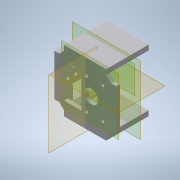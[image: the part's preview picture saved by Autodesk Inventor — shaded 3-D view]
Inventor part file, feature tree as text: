
AUTODESK INVENTOR PART (.ipt)
format: ipt  version: 2022 (Build 260153000, 153)  size: 446,976 bytes
history: native  units: mm
features: other x11, reference x11, sketch x10, plane x9, extrude x9, projected_geometry x4, hole x2, chamfer x1, pattern_linear x1
ambient origin geometry x8: Origin, YZ Plane, XZ Plane, XY Plane, X Axis, Y Axis, Z Axis, Center Point
bodies: Solid1 (feature_tree)
feature tree (58):
  plane  "Work Plane1"
  extrude  "Extrusion1"  Depth=3.0mm
  chamfer  "Chamfer1"  Distance=3.0mm
  sketch  "Sketch2"  dims[d10=3.9mm d11=2.0mm d12=45.0deg d14=31.5mm d15=0.0mm]
  plane  "Work Plane2"
  extrude  "Extrusion2"  Depth=31.5mm TaperAngle=0.0deg
  sketch  "Sketch4"  dims[d22=7.88mm d23=0.0mm d24=2.0mm]
  plane  "Work Plane3"
  extrude  "Extrusion4"  Depth=7.88mm
  extrude  "Extrusion5"  Depth=2.8mm
  pattern_linear  "Rectangular Pattern1"  Count1=5 Spacing1=6.25mm
  plane  "Work Plane4"
  hole  "Hole2"  [1 undecoded]
  plane  "Work Plane6"
  plane  "Work Plane5"
  plane  "Work Plane7"
  plane  "Work Plane8"
  extrude  "Extrusion14"  TaperAngle=0.0deg  [1 undecoded]
  extrude  "Extrusion15"  Depth=34.0mm TaperAngle=0.0deg
  extrude  "Extrusion16"  Depth=4.0mm
  extrude  "Extrusion21"  Depth=3.0mm
  plane  "Arbeitsebene9"
  extrude  "Extrusion25"  Depth=4.0mm TaperAngle=0.0deg
  other  "Arbeitspunkt1"
  hole  "Bohrung4"  [1 undecoded]
  sketch  "Sketch1"  dims[d6=3.0mm d7=3.0mm d8=3.0mm d9=0.0mm]
  projected_geometry  "Projected Loop1"
  reference  "Reference9"
  reference  "Reference10"
  reference  "Reference11"
  sketch  "Sketch12"  dims[d25=2.8mm d26=2.8mm]
  reference  "Reference23"
  reference  "Reference32"
  reference  "Reference34"
  reference  "Reference35"
  sketch  "Skizze18"  dims[d27=10.0mm d28=0.0mm d29=50.0mm d31=6.25mm]
  projected_geometry  "Projizierte Kontur10"
  sketch  "Skizze19"  dims[d56=2.8mm d57=6.0mm d58=6.0mm d59=3.0mm d60=90.0deg d61=8.0mm d62=20.594885mm d86=49.7mm]
  sketch  "Skizze20"  dims[d87=24.85mm d88=0.0mm]
  reference  "Referenz44"
  reference  "Referenz45"
  sketch  "Skizze25"  dims[d100=10.0mm d101=0.0mm d102=34.0mm d103=0.0mm]
  projected_geometry  "Projizierte Kontur14"
  sketch  "Skizze29"  dims[d104=4.0mm d105=4.0mm]
  reference  "Referenz47"
  reference  "Referenz50"
  sketch  "Skizze31"  dims[d106=34.0mm d107=0.0mm d115=3.0mm d129=4.0mm d130=0.0mm d140=8.0mm d146=10.0mm d147=0.0mm d152=11.0mm d153=13.0mm d154=25.0mm d155=11.0mm d156=3.0mm d157=6.0mm d158=6.5mm d159=4.0mm d160=90.0deg d161=8.0mm d162=20.594885mm d116=0.872665mm d117=0.5mm d118=0.872665mm]
  projected_geometry  "Projizierte Kontur15"
  other  "Assembly_Cube_Z_Focus_MGN_NEMA_v3.iam"
  other  "00_MGN12 LINEAR GUIDE RAIL, CONFIGURABLE:1"
  other  "Assembly_Cube_empty_IM_v3:1"
  other  "10_Cube_1x1_IM:1"
  other  "Assembly_Cube_empty_IM_v3:2"
  other  "10_Cube_1x1_IM:2"
  other  "30_Cube_Z_Focus_MGN_NEMA_Motoradapter_NEMA11_v3:1"
  other  "Assembly_Cube_Z-Stage_NEMA8_captive_v0.iam"
  other  "00_MGN12H, LINEAR GUIDE BLOCK:1"
  other  "00_Joy-IT-B20SHD4353_NEMA8_captive:1"
note: 3 required parameter values undecoded (feature->parameter linkage not recoverable at this tier; creation-order binding heuristic only, values carry confidence <= 0.55)
